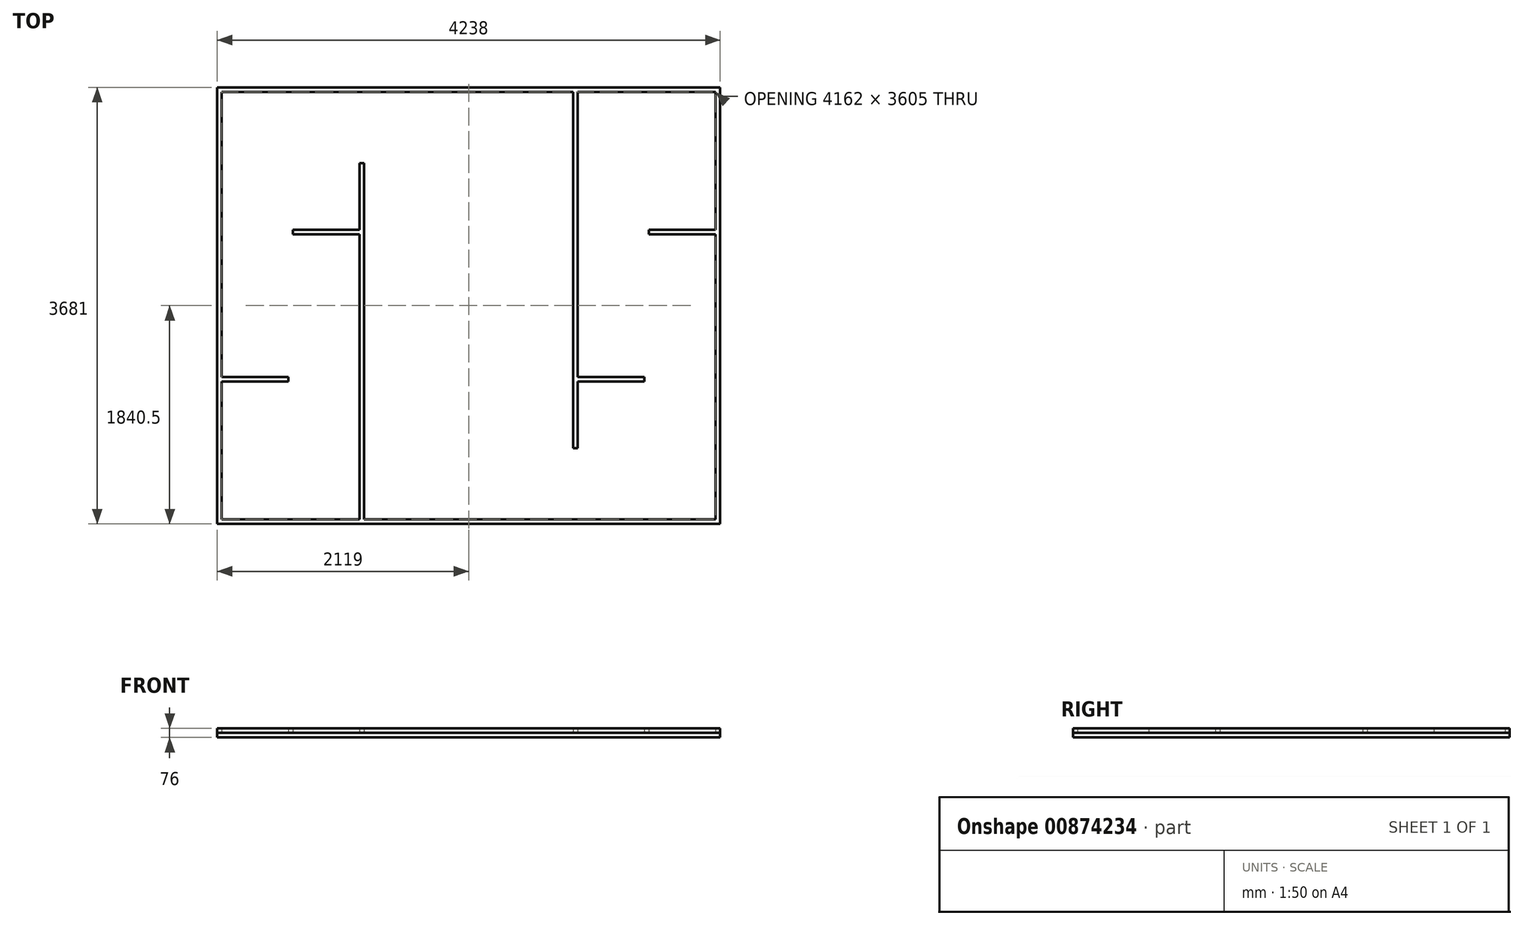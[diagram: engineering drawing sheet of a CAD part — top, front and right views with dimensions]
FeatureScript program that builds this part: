
annotation { "Feature Type Name" : "Feature", "Feature Type Description" : "" }
export const myFeature = defineFeature(function(context is Context, id is Id, definition is map)
    precondition{}
    {
        {
            var Q0;
            Q0=qCreatedBy(makeId("Top.planeOp"),FACE);
            var sketch = newSketch(context, id + "F0", { "sketchPlane" : qUnion([Q0])});
            skLineSegment(sketch, "E0.bottom", {"start": v(2119, -1840.5) * mm, "end": v(-2119, -1840.5) * mm});
            skLineSegment(sketch, "E0.top", {"start": v(2119, 1840.5) * mm, "end": v(-2119, 1840.5) * mm});
            skLineSegment(sketch, "E0.left", {"start": v(2119, -1840.5) * mm, "end": v(2119, 1840.5) * mm});
            skLineSegment(sketch, "E0.right", {"start": v(-2119, -1840.5) * mm, "end": v(-2119, 1840.5) * mm});
            skPoint(sketch, "E0.middle", {"position": v(0, 0) * mm});
            skLineSegment(sketch, "E1.bottom", {"start": v(2081, -1802.5) * mm, "end": v(-2081, -1802.5) * mm});
            skLineSegment(sketch, "E1.top", {"start": v(2081, 1802.5) * mm, "end": v(-2081, 1802.5) * mm});
            skLineSegment(sketch, "E1.left", {"start": v(2081, -1802.5) * mm, "end": v(2081, 1802.5) * mm});
            skLineSegment(sketch, "E1.right", {"start": v(-2081, -1802.5) * mm, "end": v(-2081, 1802.5) * mm});
            skLineSegment(sketch, "E2", {"start": v(2081, -1802.5) * mm, "end": v(2119, -1802.5) * mm});
            skLineSegment(sketch, "E3", {"start": v(919, 1840.5) * mm, "end": v(919, -1840.5) * mm});
            skLineSegment(sketch, "E4", {"start": v(-2119, -640.5) * mm, "end": v(2119, -640.5) * mm});
            skLineSegment(sketch, "E5", {"start": v(881, 1840.5) * mm, "end": v(881, -1840.5) * mm});
            skLineSegment(sketch, "E6", {"start": v(-2119, -602.5) * mm, "end": v(2119, -602.5) * mm});
            skLineSegment(sketch, "E7.MirrorCS", {"start": v(-881, 1840.5) * mm, "end": v(-881, -1840.5) * mm});
            skLineSegment(sketch, "E8.MirrorCS", {"start": v(-919, 1840.5) * mm, "end": v(-919, -1840.5) * mm});
            skLineSegment(sketch, "E9.MirrorCS", {"start": v(-2119, 602.5) * mm, "end": v(2119, 602.5) * mm});
            skLineSegment(sketch, "E10.MirrorCS", {"start": v(-2119, 640.5) * mm, "end": v(2119, 640.5) * mm});
            skLineSegment(sketch, "E11", {"start": v(-881, -121.5) * mm, "end": v(881, -121.5) * mm});
            skLineSegment(sketch, "E12", {"start": v(919, -40.5) * mm, "end": v(2081, -40.5) * mm});
            skLineSegment(sketch, "E13", {"start": v(1481, -640.5) * mm, "end": v(1481, -602.5) * mm});
            skLineSegment(sketch, "E14", {"start": v(1519, 640.5) * mm, "end": v(1519, 602.5) * mm});
            skLineSegment(sketch, "E15.MirrorCS", {"start": v(-881, 121.5) * mm, "end": v(881, 121.5) * mm});
            skLineSegment(sketch, "E16.MirrorCS", {"start": v(919, 40.5) * mm, "end": v(2081, 40.5) * mm});
            skLineSegment(sketch, "E17.MirrorCS", {"start": v(-919, 40.5) * mm, "end": v(-2081, 40.5) * mm});
            skLineSegment(sketch, "E18.MirrorCS", {"start": v(-919, -40.5) * mm, "end": v(-2081, -40.5) * mm});
            skLineSegment(sketch, "E19.MirrorCS", {"start": v(-1481, 640.5) * mm, "end": v(-1481, 602.5) * mm});
            skLineSegment(sketch, "E20.MirrorCS", {"start": v(-1519, -640.5) * mm, "end": v(-1519, -602.5) * mm});
            skLineSegment(sketch, "E21.bottom", {"start": v(881, -1202.5) * mm, "end": v(281, -1202.5) * mm});
            skLineSegment(sketch, "E21.top", {"start": v(881, -1802.5) * mm, "end": v(281, -1802.5) * mm});
            skLineSegment(sketch, "E21.left", {"start": v(881, -1202.5) * mm, "end": v(881, -1802.5) * mm});
            skLineSegment(sketch, "E21.right", {"start": v(281, -1202.5) * mm, "end": v(281, -1802.5) * mm});
            skLineSegment(sketch, "E22.bottom", {"start": v(881, -1802.5) * mm, "end": v(243, -1802.5) * mm});
            skLineSegment(sketch, "E22.top", {"start": v(881, -1164.5) * mm, "end": v(243, -1164.5) * mm});
            skLineSegment(sketch, "E22.left", {"start": v(881, -1802.5) * mm, "end": v(881, -1164.5) * mm});
            skLineSegment(sketch, "E22.right", {"start": v(243, -1802.5) * mm, "end": v(243, -1164.5) * mm});
            skLineSegment(sketch, "E23.bottom", {"start": v(919, -1802.5) * mm, "end": v(1519, -1802.5) * mm});
            skLineSegment(sketch, "E23.top", {"start": v(919, -1202.5) * mm, "end": v(1519, -1202.5) * mm});
            skLineSegment(sketch, "E23.left", {"start": v(919, -1802.5) * mm, "end": v(919, -1202.5) * mm});
            skLineSegment(sketch, "E23.right", {"start": v(1519, -1802.5) * mm, "end": v(1519, -1202.5) * mm});
            skLineSegment(sketch, "E24.bottom", {"start": v(919, -1802.5) * mm, "end": v(1557, -1802.5) * mm});
            skLineSegment(sketch, "E24.top", {"start": v(919, -1164.5) * mm, "end": v(1557, -1164.5) * mm});
            skLineSegment(sketch, "E24.left", {"start": v(919, -1802.5) * mm, "end": v(919, -1164.5) * mm});
            skLineSegment(sketch, "E24.right", {"start": v(1557, -1802.5) * mm, "end": v(1557, -1164.5) * mm});
            skLineSegment(sketch, "E25.bottom", {"start": v(-919, 1802.5) * mm, "end": v(-1519, 1802.5) * mm});
            skLineSegment(sketch, "E25.top", {"start": v(-919, 1202.5) * mm, "end": v(-1519, 1202.5) * mm});
            skLineSegment(sketch, "E25.left", {"start": v(-919, 1802.5) * mm, "end": v(-919, 1202.5) * mm});
            skLineSegment(sketch, "E25.right", {"start": v(-1519, 1802.5) * mm, "end": v(-1519, 1202.5) * mm});
            skLineSegment(sketch, "E26.bottom", {"start": v(-919, 1802.5) * mm, "end": v(-1557, 1802.5) * mm});
            skLineSegment(sketch, "E26.top", {"start": v(-919, 1164.5) * mm, "end": v(-1557, 1164.5) * mm});
            skLineSegment(sketch, "E26.left", {"start": v(-919, 1802.5) * mm, "end": v(-919, 1164.5) * mm});
            skLineSegment(sketch, "E26.right", {"start": v(-1557, 1802.5) * mm, "end": v(-1557, 1164.5) * mm});
            skLineSegment(sketch, "E27.bottom", {"start": v(-881, 1802.5) * mm, "end": v(-281, 1802.5) * mm});
            skLineSegment(sketch, "E27.top", {"start": v(-881, 1202.5) * mm, "end": v(-281, 1202.5) * mm});
            skLineSegment(sketch, "E27.left", {"start": v(-881, 1802.5) * mm, "end": v(-881, 1202.5) * mm});
            skLineSegment(sketch, "E27.right", {"start": v(-281, 1802.5) * mm, "end": v(-281, 1202.5) * mm});
            skLineSegment(sketch, "E28.bottom", {"start": v(-881, 1802.5) * mm, "end": v(-243, 1802.5) * mm});
            skLineSegment(sketch, "E28.top", {"start": v(-881, 1164.5) * mm, "end": v(-243, 1164.5) * mm});
            skLineSegment(sketch, "E28.left", {"start": v(-881, 1802.5) * mm, "end": v(-881, 1164.5) * mm});
            skLineSegment(sketch, "E28.right", {"start": v(-243, 1802.5) * mm, "end": v(-243, 1164.5) * mm});
            skLineSegment(sketch, "E29", {"start": v(-919, 1202.5) * mm, "end": v(-881, 1202.5) * mm});
            skLineSegment(sketch, "E30", {"start": v(881, -1202.5) * mm, "end": v(919, -1202.5) * mm});
            skSolve(sketch);
        }
        {
            var Q0;
            Q0=qCreatedBy(makeId("Top.planeOp"),FACE);
            var sketch = newSketch(context, id + "F1", { "sketchPlane" : qUnion([Q0])});
            skLineSegment(sketch, "E31.bottom", {"start": v(2119, -1840.5) * mm, "end": v(-2119, -1840.5) * mm});
            skLineSegment(sketch, "E31.top", {"start": v(2119, 1840.5) * mm, "end": v(-2119, 1840.5) * mm});
            skLineSegment(sketch, "E31.left", {"start": v(2119, -1840.5) * mm, "end": v(2119, 1840.5) * mm});
            skLineSegment(sketch, "E31.right", {"start": v(-2119, -1840.5) * mm, "end": v(-2119, 1840.5) * mm});
            skPoint(sketch, "E31.middle", {"position": v(0, 0) * mm});
            skSolve(sketch);
        }
        {
            var Q0;
            Q0 = qSketchRegion(id + "F1", true);
            extrude(context, id + "F2", {"entities" : qUnion([Q0]), "oppositeDirection" : true, "depth" : 38 * mm, "offsetDistance" : 25 * mm});
        }
        {
            var Q0;
            {var subQ5=sQuery(id+"F0.wireOp",EDGE,"E0.right");var subQ6=sQuery(id+"F0.wireOp",EDGE,"E0.top");var subQ7=makeQuery(id+"F0.imprint","INTERSECT",VERTEX,{"derivedFrom":[subQ6,subQ5]});Q0=makeQuery(id+"F0.imprint","IMPRINT",FACE,{"disambiguationData":[TD([[makeQuery(id+"F0.imprint","IMPRINT",EDGE,{"disambiguationData":[TD([[subQ7,1.0]])],"derivedFrom":subQ6}),1.0]])]});}
            var Q1;
            {var subQ0=sQuery(id+"F0.wireOp",EDGE,"E7.MirrorCS");var subQ1=sQuery(id+"F0.wireOp",EDGE,"E0.top");var subQ2=makeQuery(id+"F0.imprint","INTERSECT",VERTEX,{"derivedFrom":[subQ1,subQ0]});Q1=makeQuery(id+"F0.imprint","IMPRINT",FACE,{"disambiguationData":[TD([[makeQuery(id+"F0.imprint","IMPRINT",EDGE,{"disambiguationData":[TD([[subQ2,-1.0]])],"derivedFrom":subQ1}),1.0]])]});}
            var Q2;
            {var subQ1=sQuery(id+"F0.wireOp",EDGE,"E0.top");var subQ7=sQuery(id+"F0.wireOp",EDGE,"E5");var subQ9=makeQuery(id+"F0.imprint","INTERSECT",VERTEX,{"derivedFrom":[subQ1,subQ7]});Q2=makeQuery(id+"F0.imprint","IMPRINT",FACE,{"disambiguationData":[TD([[makeQuery(id+"F0.imprint","IMPRINT",EDGE,{"disambiguationData":[TD([[subQ9,-1.0]])],"derivedFrom":subQ1}),1.0]])]});}
            var Q3;
            {var subQ5=sQuery(id+"F0.wireOp",EDGE,"E29");Q3=makeQuery(id+"F0.imprint","IMPRINT",FACE,{"disambiguationData":[TD([[makeQuery(id+"F0.imprint","IMPRINT",EDGE,{"derivedFrom":subQ5}),-1.0]])]});}
            var Q4;
            {var subQ0=sQuery(id+"F0.wireOp",EDGE,"E9.MirrorCS");var subQ1=sQuery(id+"F0.wireOp",EDGE,"E0.right");var subQ2=makeQuery(id+"F0.imprint","INTERSECT",VERTEX,{"derivedFrom":[subQ1,subQ0]});Q4=makeQuery(id+"F0.imprint","IMPRINT",FACE,{"disambiguationData":[TD([[makeQuery(id+"F0.imprint","IMPRINT",EDGE,{"disambiguationData":[TD([[subQ2,-1.0]])],"derivedFrom":subQ1}),-1.0]])]});}
            var Q5;
            {var subQ2=sQuery(id+"F0.wireOp",EDGE,"E6");var subQ4=sQuery(id+"F0.wireOp",EDGE,"E0.right");var subQ5=makeQuery(id+"F0.imprint","INTERSECT",VERTEX,{"derivedFrom":[subQ4,subQ2]});Q5=makeQuery(id+"F0.imprint","IMPRINT",FACE,{"disambiguationData":[TD([[makeQuery(id+"F0.imprint","IMPRINT",EDGE,{"disambiguationData":[TD([[subQ5,-1.0]])],"derivedFrom":subQ4}),-1.0]])]});}
            var Q6;
            {var subQ5=sQuery(id+"F0.wireOp",EDGE,"E19.MirrorCS");Q6=makeQuery(id+"F0.imprint","IMPRINT",FACE,{"disambiguationData":[TD([[makeQuery(id+"F0.imprint","IMPRINT",EDGE,{"derivedFrom":subQ5}),1.0]])]});}
            var Q7;
            {var subQ0=sQuery(id+"F0.wireOp",EDGE,"E20.MirrorCS");Q7=makeQuery(id+"F0.imprint","IMPRINT",FACE,{"disambiguationData":[TD([[makeQuery(id+"F0.imprint","IMPRINT",EDGE,{"derivedFrom":subQ0}),1.0]])]});}
            var Q8;
            {var subQ0=sQuery(id+"F0.wireOp",EDGE,"E4");var subQ1=sQuery(id+"F0.wireOp",EDGE,"E0.right");var subQ2=makeQuery(id+"F0.imprint","INTERSECT",VERTEX,{"derivedFrom":[subQ1,subQ0]});Q8=makeQuery(id+"F0.imprint","IMPRINT",FACE,{"disambiguationData":[TD([[makeQuery(id+"F0.imprint","IMPRINT",EDGE,{"disambiguationData":[TD([[subQ2,-1.0]])],"derivedFrom":subQ1}),-1.0]])]});}
            var Q9;
            {var subQ1=sQuery(id+"F0.wireOp",EDGE,"E0.right");var subQ5=sQuery(id+"F0.wireOp",EDGE,"E0.bottom");var subQ6=makeQuery(id+"F0.imprint","INTERSECT",VERTEX,{"derivedFrom":[subQ5,subQ1]});Q9=makeQuery(id+"F0.imprint","IMPRINT",FACE,{"disambiguationData":[TD([[makeQuery(id+"F0.imprint","IMPRINT",EDGE,{"disambiguationData":[TD([[subQ6,1.0]])],"derivedFrom":subQ5}),-1.0]])]});}
            var Q10;
            {var subQ0=sQuery(id+"F0.wireOp",EDGE,"E8.MirrorCS");var subQ1=sQuery(id+"F0.wireOp",EDGE,"E4");var subQ2=makeQuery(id+"F0.imprint","INTERSECT",VERTEX,{"derivedFrom":[subQ1,subQ0]});Q10=makeQuery(id+"F0.imprint","IMPRINT",FACE,{"disambiguationData":[TD([[makeQuery(id+"F0.imprint","IMPRINT",EDGE,{"disambiguationData":[TD([[subQ2,-1.0]])],"derivedFrom":subQ1}),1.0]])]});}
            var Q11;
            {var subQ2=sQuery(id+"F0.wireOp",EDGE,"E6");var subQ4=sQuery(id+"F0.wireOp",EDGE,"E8.MirrorCS");var subQ5=makeQuery(id+"F0.imprint","INTERSECT",VERTEX,{"derivedFrom":[subQ2,subQ4]});Q11=makeQuery(id+"F0.imprint","IMPRINT",FACE,{"disambiguationData":[TD([[makeQuery(id+"F0.imprint","IMPRINT",EDGE,{"disambiguationData":[TD([[subQ5,-1.0]])],"derivedFrom":subQ2}),1.0]])]});}
            var Q12;
            {var subQ0=sQuery(id+"F0.wireOp",EDGE,"E10.MirrorCS");var subQ1=sQuery(id+"F0.wireOp",EDGE,"E7.MirrorCS");var subQ2=makeQuery(id+"F0.imprint","INTERSECT",VERTEX,{"derivedFrom":[subQ1,subQ0]});Q12=makeQuery(id+"F0.imprint","IMPRINT",FACE,{"disambiguationData":[TD([[makeQuery(id+"F0.imprint","IMPRINT",EDGE,{"disambiguationData":[TD([[subQ2,-1.0]])],"derivedFrom":subQ1}),-1.0]])]});}
            var Q13;
            {var subQ0=sQuery(id+"F0.wireOp",EDGE,"E7.MirrorCS");var subQ1=sQuery(id+"F0.wireOp",EDGE,"E1.bottom");var subQ2=makeQuery(id+"F0.imprint","INTERSECT",VERTEX,{"derivedFrom":[subQ1,subQ0]});Q13=makeQuery(id+"F0.imprint","IMPRINT",FACE,{"disambiguationData":[TD([[makeQuery(id+"F0.imprint","IMPRINT",EDGE,{"disambiguationData":[TD([[subQ2,-1.0]])],"derivedFrom":subQ1}),-1.0]])]});}
            var Q14;
            {var subQ0=sQuery(id+"F0.wireOp",EDGE,"E7.MirrorCS");var subQ1=sQuery(id+"F0.wireOp",EDGE,"E0.bottom");var subQ2=makeQuery(id+"F0.imprint","INTERSECT",VERTEX,{"derivedFrom":[subQ1,subQ0]});Q14=makeQuery(id+"F0.imprint","IMPRINT",FACE,{"disambiguationData":[TD([[makeQuery(id+"F0.imprint","IMPRINT",EDGE,{"disambiguationData":[TD([[subQ2,-1.0]])],"derivedFrom":subQ1}),-1.0]])]});}
            var Q15;
            {var subQ0=sQuery(id+"F0.wireOp",EDGE,"E5");var subQ1=sQuery(id+"F0.wireOp",EDGE,"E0.bottom");var subQ2=makeQuery(id+"F0.imprint","INTERSECT",VERTEX,{"derivedFrom":[subQ1,subQ0]});Q15=makeQuery(id+"F0.imprint","IMPRINT",FACE,{"disambiguationData":[TD([[makeQuery(id+"F0.imprint","IMPRINT",EDGE,{"disambiguationData":[TD([[subQ2,-1.0]])],"derivedFrom":subQ1}),-1.0]])]});}
            var Q16;
            {var subQ0=sQuery(id+"F0.wireOp",EDGE,"E2");Q16=makeQuery(id+"F0.imprint","IMPRINT",FACE,{"disambiguationData":[TD([[makeQuery(id+"F0.imprint","IMPRINT",EDGE,{"derivedFrom":subQ0}),-1.0]])]});}
            var Q17;
            {var subQ0=sQuery(id+"F0.wireOp",EDGE,"E4");var subQ1=sQuery(id+"F0.wireOp",EDGE,"E0.left");var subQ2=makeQuery(id+"F0.imprint","INTERSECT",VERTEX,{"derivedFrom":[subQ1,subQ0]});Q17=makeQuery(id+"F0.imprint","IMPRINT",FACE,{"disambiguationData":[TD([[makeQuery(id+"F0.imprint","IMPRINT",EDGE,{"disambiguationData":[TD([[subQ2,-1.0]])],"derivedFrom":subQ1}),1.0]])]});}
            var Q18;
            {var subQ4=sQuery(id+"F0.wireOp",EDGE,"E6");var subQ5=sQuery(id+"F0.wireOp",EDGE,"E0.left");var subQ6=makeQuery(id+"F0.imprint","INTERSECT",VERTEX,{"derivedFrom":[subQ5,subQ4]});Q18=makeQuery(id+"F0.imprint","IMPRINT",FACE,{"disambiguationData":[TD([[makeQuery(id+"F0.imprint","IMPRINT",EDGE,{"disambiguationData":[TD([[subQ6,-1.0]])],"derivedFrom":subQ5}),1.0]])]});}
            var Q19;
            {var subQ0=sQuery(id+"F0.wireOp",EDGE,"E6");var subQ1=sQuery(id+"F0.wireOp",EDGE,"E3");var subQ2=makeQuery(id+"F0.imprint","INTERSECT",VERTEX,{"derivedFrom":[subQ1,subQ0]});Q19=makeQuery(id+"F0.imprint","IMPRINT",FACE,{"disambiguationData":[TD([[makeQuery(id+"F0.imprint","IMPRINT",EDGE,{"disambiguationData":[TD([[subQ2,-1.0]])],"derivedFrom":subQ1}),-1.0]])]});}
            var Q20;
            {var subQ0=sQuery(id+"F0.wireOp",EDGE,"E10.MirrorCS");var subQ1=sQuery(id+"F0.wireOp",EDGE,"E3");var subQ2=makeQuery(id+"F0.imprint","INTERSECT",VERTEX,{"derivedFrom":[subQ1,subQ0]});Q20=makeQuery(id+"F0.imprint","IMPRINT",FACE,{"disambiguationData":[TD([[makeQuery(id+"F0.imprint","IMPRINT",EDGE,{"disambiguationData":[TD([[subQ2,-1.0]])],"derivedFrom":subQ1}),-1.0]])]});}
            var Q21;
            {var subQ0=sQuery(id+"F0.wireOp",EDGE,"E3");var subQ1=sQuery(id+"F0.wireOp",EDGE,"E1.top");var subQ2=makeQuery(id+"F0.imprint","INTERSECT",VERTEX,{"derivedFrom":[subQ1,subQ0]});Q21=makeQuery(id+"F0.imprint","IMPRINT",FACE,{"disambiguationData":[TD([[makeQuery(id+"F0.imprint","IMPRINT",EDGE,{"disambiguationData":[TD([[subQ2,-1.0]])],"derivedFrom":subQ1}),1.0]])]});}
            var Q22;
            {var subQ7=sQuery(id+"F0.wireOp",EDGE,"E0.left");var subQ8=sQuery(id+"F0.wireOp",EDGE,"E0.top");var subQ9=makeQuery(id+"F0.imprint","INTERSECT",VERTEX,{"derivedFrom":[subQ8,subQ7]});Q22=makeQuery(id+"F0.imprint","IMPRINT",FACE,{"disambiguationData":[TD([[makeQuery(id+"F0.imprint","IMPRINT",EDGE,{"disambiguationData":[TD([[subQ9,-1.0]])],"derivedFrom":subQ8}),1.0]])]});}
            var Q23;
            {var subQ5=sQuery(id+"F0.wireOp",EDGE,"E13");Q23=makeQuery(id+"F0.imprint","IMPRINT",FACE,{"disambiguationData":[TD([[makeQuery(id+"F0.imprint","IMPRINT",EDGE,{"derivedFrom":subQ5}),1.0]])]});}
            var Q24;
            {var subQ0=sQuery(id+"F0.wireOp",EDGE,"E3");var subQ1=sQuery(id+"F0.wireOp",EDGE,"E0.bottom");var subQ2=makeQuery(id+"F0.imprint","INTERSECT",VERTEX,{"derivedFrom":[subQ1,subQ0]});Q24=makeQuery(id+"F0.imprint","IMPRINT",FACE,{"disambiguationData":[TD([[makeQuery(id+"F0.imprint","IMPRINT",EDGE,{"disambiguationData":[TD([[subQ2,-1.0]])],"derivedFrom":subQ1}),-1.0]])]});}
            var Q25;
            {var subQ0=sQuery(id+"F0.wireOp",EDGE,"E9.MirrorCS");var subQ1=sQuery(id+"F0.wireOp",EDGE,"E0.left");var subQ2=makeQuery(id+"F0.imprint","INTERSECT",VERTEX,{"derivedFrom":[subQ1,subQ0]});Q25=makeQuery(id+"F0.imprint","IMPRINT",FACE,{"disambiguationData":[TD([[makeQuery(id+"F0.imprint","IMPRINT",EDGE,{"disambiguationData":[TD([[subQ2,-1.0]])],"derivedFrom":subQ1}),1.0]])]});}
            var Q26;
            {var subQ3=sQuery(id+"F0.wireOp",EDGE,"E4");var subQ5=sQuery(id+"F0.wireOp",EDGE,"E3");var subQ6=makeQuery(id+"F0.imprint","INTERSECT",VERTEX,{"derivedFrom":[subQ5,subQ3]});Q26=makeQuery(id+"F0.imprint","IMPRINT",FACE,{"disambiguationData":[TD([[makeQuery(id+"F0.imprint","IMPRINT",EDGE,{"disambiguationData":[TD([[subQ6,1.0]])],"derivedFrom":subQ3}),-1.0]])]});}
            var Q27;
            {var subQ5=sQuery(id+"F0.wireOp",EDGE,"E14");Q27=makeQuery(id+"F0.imprint","IMPRINT",FACE,{"disambiguationData":[TD([[makeQuery(id+"F0.imprint","IMPRINT",EDGE,{"derivedFrom":subQ5}),1.0]])]});}
            var Q28;
            {var subQ0=sQuery(id+"F0.wireOp",EDGE,"E2");Q28=makeQuery(id+"F0.imprint","IMPRINT",FACE,{"disambiguationData":[TD([[makeQuery(id+"F0.imprint","IMPRINT",EDGE,{"derivedFrom":subQ0}),1.0]])]});}
            var Q29;
            {var subQ5=sQuery(id+"F0.wireOp",EDGE,"E3");var subQ9=makeQuery(id+"F0.imprint","INTERSECT",VERTEX,{"derivedFrom":[subQ5,sQuery(id+"F0.wireOp",EDGE,"E16.MirrorCS")]});Q29=makeQuery(id+"F0.imprint","IMPRINT",FACE,{"disambiguationData":[TD([[makeQuery(id+"F0.imprint","IMPRINT",EDGE,{"disambiguationData":[TD([[subQ9,1.0]])],"derivedFrom":subQ5}),-1.0]])]});}
            var Q30;
            {var subQ0=sQuery(id+"F0.wireOp",EDGE,"E3");var subQ1=sQuery(id+"F0.wireOp",EDGE,"E0.top");var subQ2=makeQuery(id+"F0.imprint","INTERSECT",VERTEX,{"derivedFrom":[subQ1,subQ0]});Q30=makeQuery(id+"F0.imprint","IMPRINT",FACE,{"disambiguationData":[TD([[makeQuery(id+"F0.imprint","IMPRINT",EDGE,{"disambiguationData":[TD([[subQ2,-1.0]])],"derivedFrom":subQ1}),1.0]])]});}
            extrude(context, id + "F3", {"entities" : qUnion([Q0, Q1, Q2, Q3, Q4, Q5, Q6, Q7, Q8, Q9, Q10, Q11, Q12, Q13, Q14, Q15, Q16, Q17, Q18, Q19, Q20, Q21, Q22, Q23, Q24, Q25, Q26, Q27, Q28, Q29, Q30]), "depth" : 38 * mm, "offsetDistance" : 25 * mm});
        }
    });
